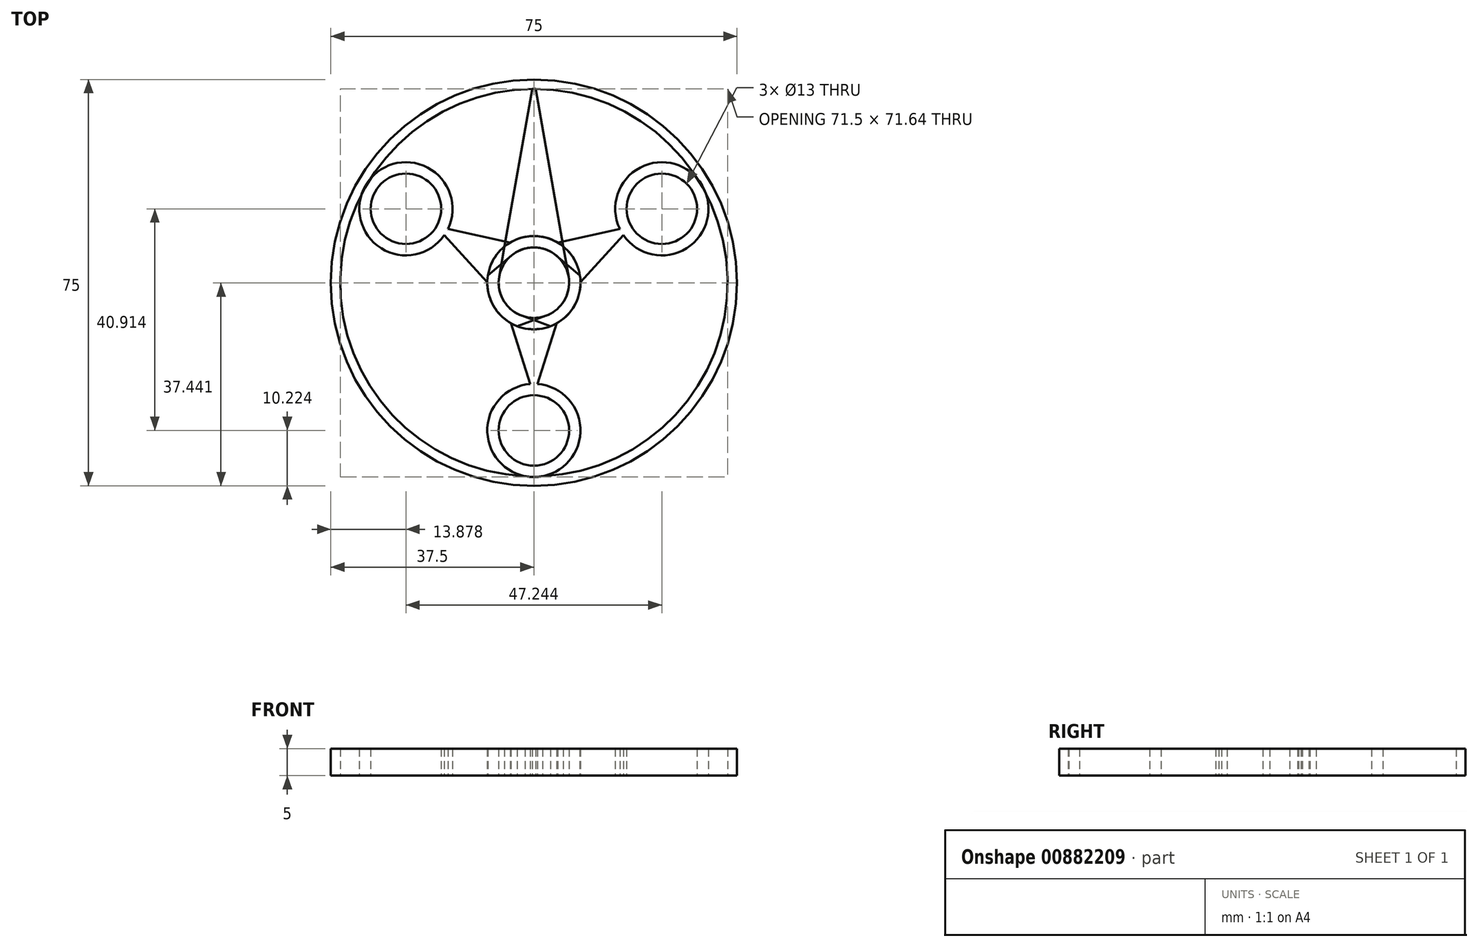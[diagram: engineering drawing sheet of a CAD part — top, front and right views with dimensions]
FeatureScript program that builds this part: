
annotation { "Feature Type Name" : "Feature", "Feature Type Description" : "" }
export const myFeature = defineFeature(function(context is Context, id is Id, definition is map)
    precondition{}
    {
        {
            var Q0;
            Q0=qCreatedBy(makeId("Top.planeOp"),FACE);
            var sketch = newSketch(context, id + "F0", { "sketchPlane" : qUnion([Q0])});
            skCircle(sketch, "E0", {"center": v(0, 0) * mm, "radius": 6.5 * mm});
            skLineSegment(sketch, "E1", {"start": v(0, 37.5) * mm, "end": v(-6.6, 0) * mm});
            skLineSegment(sketch, "E2", {"start": v(-6.6, 0) * mm, "end": v(0, 37.5) * mm});
            skLineSegment(sketch, "E3", {"start": v(0, 37.5) * mm, "end": v(6.6, 0) * mm});
            skPoint(sketch, "E4.startSnap0", {"position": v(-3.3, 18.75) * mm});
            skCircle(sketch, "E5", {"center": v(0, 0) * mm, "radius": 8.6 * mm});
            skCircle(sketch, "E6", {"center": v(0, 0) * mm, "radius": 35.76 * mm});
            skCircle(sketch, "E7", {"center": v(0, 0) * mm, "radius": 37.5 * mm});
            skCircle(sketch, "E8", {"center": v(0, -27.28) * mm, "radius": 8.6 * mm});
            skCircle(sketch, "E9", {"center": v(0, -27.28) * mm, "radius": 6.5 * mm});
            skLineSegment(sketch, "E10", {"start": v(-6.6, 0) * mm, "end": v(0, -20.78) * mm});
            skLineSegment(sketch, "E11", {"start": v(0, -20.78) * mm, "end": v(6.6, 0) * mm});
            skSolve(sketch);
        }
        {
            var Q0;
            {var subQ1=sQuery(id+"F0.wireOp",EDGE,"E2");var subQ3=sQuery(id+"F0.wireOp",EDGE,"E5");var subQ4=makeQuery(id+"F0.imprint","INTERSECT",VERTEX,{"derivedFrom":[subQ1,subQ3]});Q0=makeQuery(id+"F0.imprint","IMPRINT",FACE,{"disambiguationData":[TD([[makeQuery(id+"F0.imprint","IMPRINT",EDGE,{"disambiguationData":[TD([[subQ4,1.0]])],"derivedFrom":subQ3}),-1.0]])]});}
            var Q1;
            {var subQ0=sQuery(id+"F0.wireOp",EDGE,"E2");var subQ1=sQuery(id+"F0.wireOp",EDGE,"E0");var subQ2=makeQuery(id+"F0.imprint","INTERSECT",VERTEX,{"derivedFrom":[subQ1,subQ0]});Q1=makeQuery(id+"F0.imprint","IMPRINT",FACE,{"disambiguationData":[TD([[makeQuery(id+"F0.imprint","IMPRINT",EDGE,{"disambiguationData":[TD([[subQ2,-1.0]])],"derivedFrom":subQ1}),-1.0]])]});}
            var Q2;
            {var subQ0=sQuery(id+"F0.wireOp",EDGE,"E2");var subQ1=sQuery(id+"F0.wireOp",EDGE,"E0");var subQ2=makeQuery(id+"F0.imprint","INTERSECT",VERTEX,{"derivedFrom":[subQ1,subQ0]});Q2=makeQuery(id+"F0.imprint","IMPRINT",FACE,{"disambiguationData":[TD([[makeQuery(id+"F0.imprint","IMPRINT",EDGE,{"disambiguationData":[TD([[subQ2,1.0]])],"derivedFrom":subQ1}),-1.0]])]});}
            var Q3;
            Q3=makeQuery(id+"F0.imprint","IMPRINT",FACE,{"disambiguationData":[TD([[makeQuery(id+"F0.imprint","IMPRINT",EDGE,{"derivedFrom":sQuery(id+"F0.wireOp",EDGE,"E9")}),-1.0]])]});
            var Q4;
            {var subQ0=sQuery(id+"F0.wireOp",EDGE,"E8");var subQ1=sQuery(id+"F0.wireOp",EDGE,"E6");var subQ2=makeQuery(id+"F0.imprint","INTERSECT",VERTEX,{"disambiguationData":[OD(0.0)],"derivedFrom":[subQ1,subQ0]});Q4=makeQuery(id+"F0.imprint","IMPRINT",FACE,{"disambiguationData":[TD([[makeQuery(id+"F0.imprint","IMPRINT",EDGE,{"disambiguationData":[TD([[subQ2,-1.0]])],"derivedFrom":subQ1}),-1.0]])]});}
            var Q5;
            {var subQ0=sQuery(id+"F0.wireOp",EDGE,"E10");var subQ1=sQuery(id+"F0.wireOp",EDGE,"E5");var subQ2=makeQuery(id+"F0.imprint","INTERSECT",VERTEX,{"derivedFrom":[subQ1,subQ0]});Q5=makeQuery(id+"F0.imprint","IMPRINT",FACE,{"disambiguationData":[TD([[makeQuery(id+"F0.imprint","IMPRINT",EDGE,{"disambiguationData":[TD([[subQ2,-1.0]])],"derivedFrom":subQ1}),-1.0]])]});}
            var Q6;
            {var subQ0=sQuery(id+"F0.wireOp",EDGE,"E11");var subQ3=sQuery(id+"F0.wireOp",EDGE,"E0");var subQ5=makeQuery(id+"F0.imprint","INTERSECT",VERTEX,{"disambiguationData":[OD(0.0)],"derivedFrom":[subQ3,subQ0]});Q6=makeQuery(id+"F0.imprint","IMPRINT",FACE,{"disambiguationData":[TD([[makeQuery(id+"F0.imprint","IMPRINT",EDGE,{"disambiguationData":[TD([[subQ5,-1.0]])],"derivedFrom":subQ3}),-1.0]])]});}
            var Q7;
            {var subQ3=sQuery(id+"F0.wireOp",EDGE,"E10");var subQ6=sQuery(id+"F0.wireOp",EDGE,"E0");var subQ8=makeQuery(id+"F0.imprint","INTERSECT",VERTEX,{"disambiguationData":[OD(0.0)],"derivedFrom":[subQ6,subQ3]});Q7=makeQuery(id+"F0.imprint","IMPRINT",FACE,{"disambiguationData":[TD([[makeQuery(id+"F0.imprint","IMPRINT",EDGE,{"disambiguationData":[TD([[subQ8,-1.0]])],"derivedFrom":subQ6}),-1.0]])]});}
            var Q8;
            {var subQ0=sQuery(id+"F0.wireOp",EDGE,"E10");var subQ1=sQuery(id+"F0.wireOp",EDGE,"E8");var subQ2=makeQuery(id+"F0.imprint","INTERSECT",VERTEX,{"derivedFrom":[subQ1,subQ0]});Q8=makeQuery(id+"F0.imprint","IMPRINT",FACE,{"disambiguationData":[TD([[makeQuery(id+"F0.imprint","IMPRINT",EDGE,{"disambiguationData":[TD([[subQ2,1.0]])],"derivedFrom":subQ1}),1.0]])]});}
            var Q9;
            {var subQ0=sQuery(id+"F0.wireOp",EDGE,"E10");var subQ1=sQuery(id+"F0.wireOp",EDGE,"E0");var subQ2=makeQuery(id+"F0.imprint","INTERSECT",VERTEX,{"disambiguationData":[OD(1.0)],"derivedFrom":[subQ1,subQ0]});Q9=makeQuery(id+"F0.imprint","IMPRINT",FACE,{"disambiguationData":[TD([[makeQuery(id+"F0.imprint","IMPRINT",EDGE,{"disambiguationData":[TD([[subQ2,-1.0]])],"derivedFrom":subQ1}),-1.0]])]});}
            extrude(context, id + "F1", {"entities" : qUnion([Q0, Q1, Q2, Q3, Q4, Q5, Q6, Q7, Q8, Q9]), "depth" : 5 * mm, "offsetDistance" : 25 * mm});
        }
        {
            var Q0;
            Q0=makeQuery(id+"F1.opExtrude","SWEPT_BODY",BODY,{"disambiguationData":[OSD([sQuery(id+"F0.wireOp",EDGE,"E0"),sQuery(id+"F0.wireOp",EDGE,"E2"),sQuery(id+"F0.wireOp",EDGE,"E3"),sQuery(id+"F0.wireOp",EDGE,"E5")])]});
            var Q1;
            Q1=makeQuery(id+"F1.opExtrude","SWEPT_BODY",BODY,{"disambiguationData":[OSD([sQuery(id+"F0.wireOp",EDGE,"E8"),sQuery(id+"F0.wireOp",EDGE,"E9")])]});
            var Q2;
            {var subQ0=sQuery(id+"F0.wireOp",EDGE,"E5");Q2=makeQuery(id+"F1.opExtrude","SWEPT_FACE",FACE,{"disambiguationData":[OSD([subQ0]),TDD([makeQuery(id+"F0.imprint","IMPRINT",EDGE,{"disambiguationData":[TD([[makeQuery(id+"F0.imprint","INTERSECT",VERTEX,{"derivedFrom":[sQuery(id+"F0.wireOp",EDGE,"E3"),subQ0]}),1.0]])],"derivedFrom":subQ0})])]});}
            circularPattern(context, id + "F2", {"entities" : qUnion([Q0, Q1]), "axis" : qUnion([Q2]), "angle" : 360 * degree, "instanceCount" : 3, "equalSpace" : true});
        }
        {
            var Q0;
            Q0 = qSketchRegion(id + "F0", true);
            extrude(context, id + "F3", {"entities" : qUnion([Q0]), "depth" : 5 * mm, "offsetDistance" : 25 * mm});
        }
    });
